# Revit family: 2023855
name_source: partatom
category: Lighting Fixtures
revit_build: Autodesk Revit 2018 (Build: 20170223_1515(x64)
units: mm (PartAtom-declared; Revit-internal decimal feet)

## family parameters
Cut with Voids When Loaded = No
Host = Face
Light Source = Yes
OmniClass Number = 23.80.70.00
OmniClass Title = Lighting
Part Type = Normal
Room Calculation Point = No
Round Connector Dimension = Use Diameter
Shared = No

## types (1)
- 2023855 OPTIX LIN S 1200 LUMI HCL TW ALU DA
    Apparent Load = 26 VA
    Assembly Code = D5020200
    AssetType = Fixed
    ClassificationName = Uniclass2015
    ClassificationValue = EF_70_80
    Color Filter = 16777215
    Cost = 0 $
    Default Elevation = 1219 mm
    Description = OPTIX LINEAR SURFACE 1200 LUMI HCL TW ALU DALI is a surface mounted linear luminaire for office and education applications with Aluminised plastic extra low glare optics and RAL9016 colour fixture body.  DALI DT8 controlled tunable white light engine.   2700-6200K Tunable White LED, chromaticity tolerance of 3-step MacAdam ellipse. For 2700K - Colour rendering index Ra >98; Melanopic Ratio MEER: 0.527; Fidelity Index Rᶠ: 97; Gamut Index Rᶢ: 102. For 4000K - Colour rendering index Ra >95; Melanopic Ratio MEER: 0.827; Fidelity Index Rᶠ: 95; Gamut Index Rᶢ: 101. For 6200K - Colour rendering index Ra >98; Melanopic Ratio MEER: 1.087; Fidelity Index Rᶠ: 96; Gamut Index Rᶢ: 99. For 4000K luminous flux: 2225lm. Power consumption: 26W. Luminaire efficacy: 86lm/W. UGR<16 Luminance at 65°<200 Cd/m2, IK07, IP20. Photobiological safety risk group 0. Electrical protection Class I. Glow wire test 850°C. 68,000hrs L80B20 lifespan.
    Dimming Lamp Color Temperature Shift = <None>
    DocumentationLiterature = http://www.sylvania-lighting.com
    ElectricShockClassification = 85
    Emit Shape Visible in Rendering = No
    Emit from Circle Diameter = 610 mm
    Height = 86 mm  [stored 0.282152 ft]
    IfcExportAs = Class I
    IfcExportType = IfcLightFixtureType
    ImpactProtectionIndex = IfcLightFixtureType
    IngressProtection = IfcLightFixtureType
    InputNominalFrequency = 4000
    InputVoltage = 0
    LampColourRenderingIndex = 16500
    LampColourTemperature = LED
    LampMacAdamStep = 95
    LampNominalLuminous = 4000 K
    Length = 1130 mm  [stored 3.70735 ft]
    LightOutputRatio = LED
    LuminaireType = 0
    ManufacturerName = 85 lm/W
    Material = Feilo Sylvania
    Material_1_SYL = <By Category>
    Material_2_SYL = <By Category>
    Material_3_SYL = <By Category>
    Material_4_SYL = <By Category>
    Model = OPTIX LINEAR SURFACE 1200 LUMI HCL TW ALU DALI
    ModelNumber = 2023855
    ModelReference = OPTIX LINEAR SURFACE 1200 LUMI HCL TW ALU DALI
    Name = OPTIX LINEAR SURFACE 1200 LUMI HCL TW ALU DALI
    NominalDepth = 0 mm  [stored 0 ft]
    NominalHeight = 0 mm  [stored 0 ft]
    NominalLength = 90 mm  [stored 0.295276 ft]
    Photometric Web File = 2023855.ies
    PowerConsumption = Lighting
    PowerFactor = 0
    Tilt Angle = -90.00°
    Type Image = <None>
    TypeName = OPTIX LINEAR SURFACE 1200 LUMI HCL TW ALU DALI
    URL = 0.95
    Voltage = 0 V
    WarrantyDescription = http://www.sylvania-lighting.com
    Width = 90 mm  [stored 0.295276 ft]

note: [stored X ft] marks values corroborated as IEEE doubles in the binary element streams (Revit-internal decimal feet)

## geometry (parser evidence)
native form markers: Sweep x2
no freeform markers — native parametric forms only
